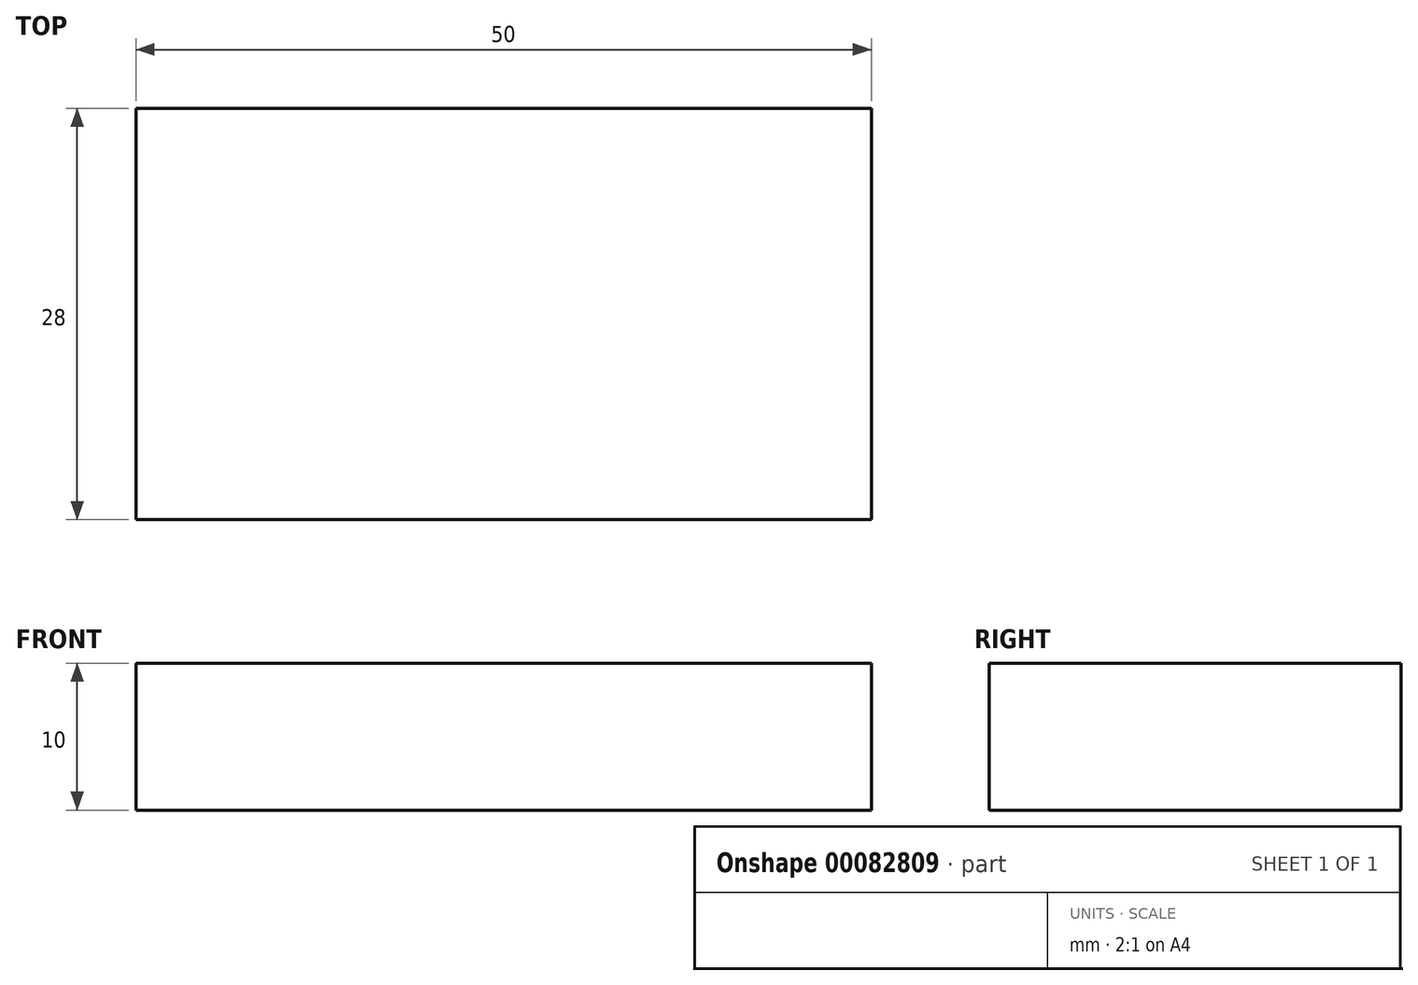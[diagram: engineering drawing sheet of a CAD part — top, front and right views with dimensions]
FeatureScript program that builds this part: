
annotation { "Feature Type Name" : "Feature", "Feature Type Description" : "" }
export const myFeature = defineFeature(function(context is Context, id is Id, definition is map)
    precondition{}
    {
        {
            var Q0;
            Q0=qCreatedBy(makeId("Top.planeOp"),FACE);
            var sketch = newSketch(context, id + "F0", { "sketchPlane" : qUnion([Q0])});
            skLineSegment(sketch, "E0.bottom", {"start": v(25, 14) * mm, "end": v(-25, 14) * mm});
            skLineSegment(sketch, "E0.top", {"start": v(25, -14) * mm, "end": v(-25, -14) * mm});
            skLineSegment(sketch, "E0.left", {"start": v(25, 14) * mm, "end": v(25, -14) * mm});
            skLineSegment(sketch, "E0.right", {"start": v(-25, 14) * mm, "end": v(-25, -14) * mm});
            skPoint(sketch, "E0.middle", {"position": v(0, 0) * mm});
            skSolve(sketch);
        }
        {
            var Q0;
            Q0 = qSketchRegion(id + "F0", true);
            extrude(context, id + "F1", {"entities" : qUnion([Q0]), "depth" : 10 * mm});
        }
    });
